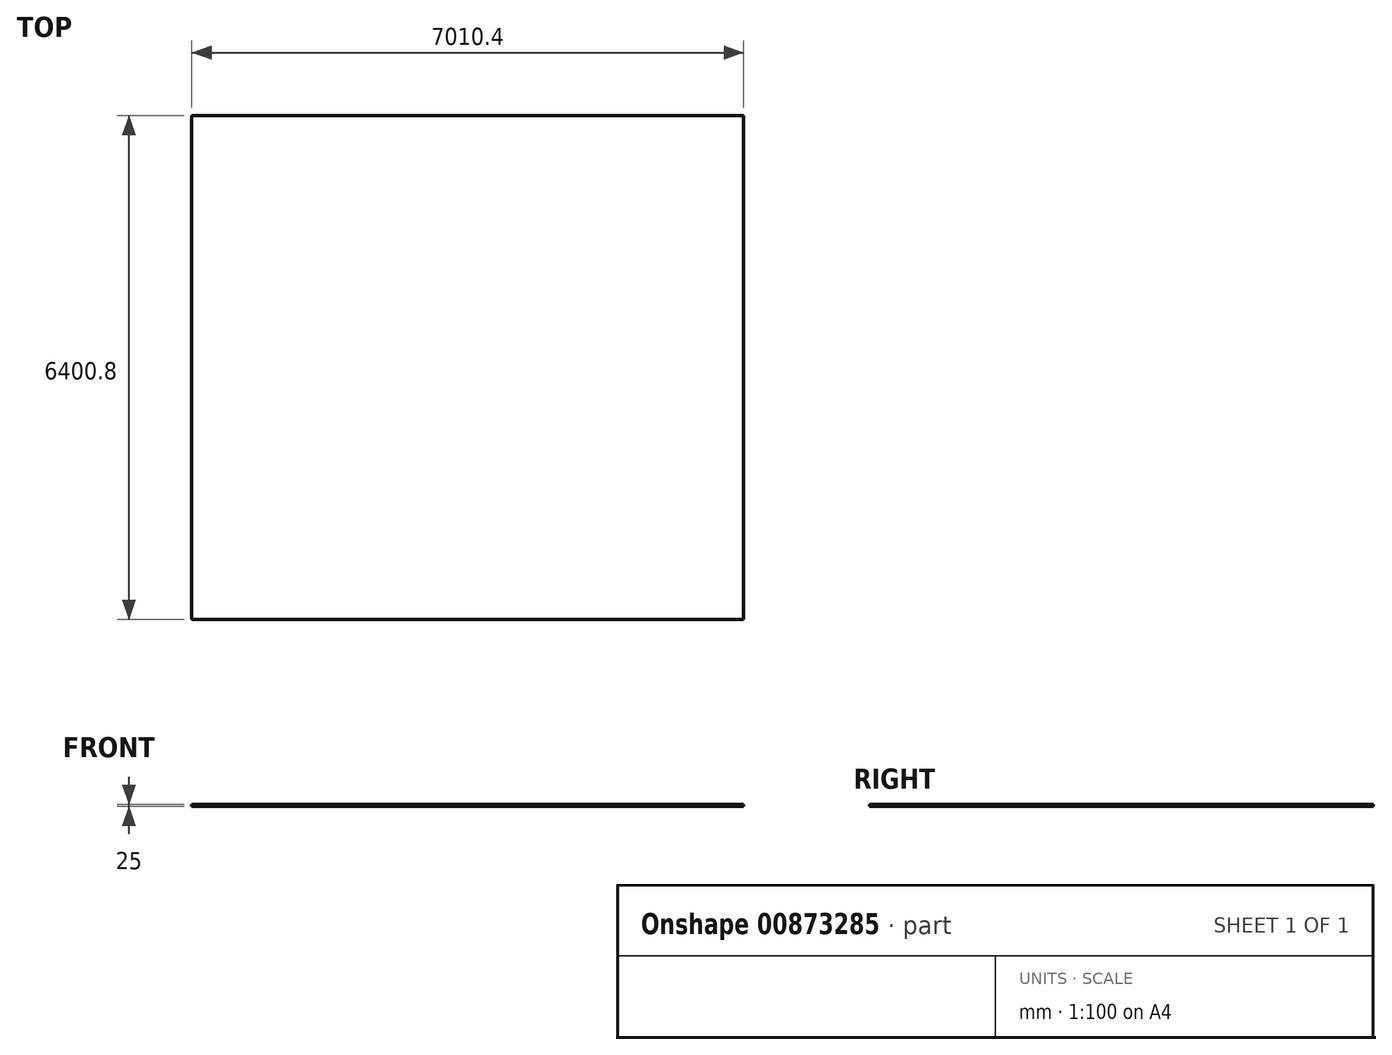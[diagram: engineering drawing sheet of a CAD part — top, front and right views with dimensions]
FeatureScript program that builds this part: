
annotation { "Feature Type Name" : "Feature", "Feature Type Description" : "" }
export const myFeature = defineFeature(function(context is Context, id is Id, definition is map)
    precondition{}
    {
        {
            var Q0;
            Q0=qCreatedBy(makeId("Top.planeOp"),FACE);
            var sketch = newSketch(context, id + "F0", { "sketchPlane" : qUnion([Q0])});
            skLineSegment(sketch, "E0.bottom", {"start": v(3505.2, -3200.4) * mm, "end": v(-3505.2, -3200.4) * mm});
            skLineSegment(sketch, "E0.top", {"start": v(3505.2, 3200.4) * mm, "end": v(-3505.2, 3200.4) * mm});
            skLineSegment(sketch, "E0.left", {"start": v(3505.2, -3200.4) * mm, "end": v(3505.2, 3200.4) * mm});
            skLineSegment(sketch, "E0.right", {"start": v(-3505.2, -3200.4) * mm, "end": v(-3505.2, 3200.4) * mm});
            skPoint(sketch, "E0.middle", {"position": v(0, 0) * mm});
            skSolve(sketch);
        }
        {
            var Q0;
            Q0=makeQuery(id+"F0.imprint","IMPRINT",FACE,{"disambiguationData":[TD([[makeQuery(id+"F0.imprint","IMPRINT",EDGE,{"derivedFrom":sQuery(id+"F0.wireOp",EDGE,"E0.bottom")}),-1.0]])]});
            extrude(context, id + "F1", {"entities" : qUnion([Q0]), "depth" : 25 * mm, "offsetDistance" : 25 * mm});
        }
    });
